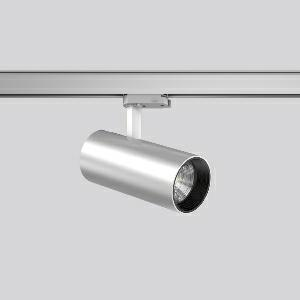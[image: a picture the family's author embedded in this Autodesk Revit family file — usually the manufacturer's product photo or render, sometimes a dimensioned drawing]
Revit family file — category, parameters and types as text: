
# Revit family: deecos_s_mini_742199_004_1_76_ead4
name_source: partatom
category: Lighting Fixtures
units: mm (PartAtom-declared; Revit-internal decimal feet)

## family parameters
Cut with Voids When Loaded = No
Host = Face
Light Source = No
Part Type = Normal
Room Calculation Point = No
Round Connector Dimension = Use Diameter
Shared = No

## types (1)
- DEECOS S mini (1 x LED Modul 940, 2250 lm, 4000)
    Apparent Load = 20 VA
    Approval mark = CE
    CIE Flux Codes = 96 100 100 100 100
    Color Rendering = 92
    Color Temperature = 4000
    Default Elevation = 1800 mm
    Description = Series: DEECOS S mini
LED surface-mounted projector in modern design with no visible cooling ribs. Housing: die-cast aluminium, powder-coated. Rotation range: 356°. Swivel range: 90°. Black plastic ring and recessed LED to prevent glare from the side. Optical assembly with lens made of plastic (polycarbonate) for the best homogeneous light distribution - can be changed without tools. Best colour rendering index Ra>90. With adapter for RZB 3-circuit DALI tracks. Suitable for Track on ceiling, Wall track. High quality converter without flickering and stroboscopic effect. The following accessories can be mounted without use of tools: interchangeable lenses, decorative glasses, honeycomb louvre, clear and frosted diffusers, white interchangeable plastic ring. 
Colour: silver
Diameter: 87 mm
Height: 214 mm
Lamp: LED
Socket: without socket
Colour temperature: 4000K
Colour rendering index (CRI): 92
System power: 20 W
Rated luminous flux: 2250 lm
Luminous efficiency: 113 lm/W
Control gear: Converter, dimmable, DALI
Protection class: I
Type of protection: IP 20
    Height = 214 mm
    Lamp = 1 x LED Modul 940
    Lamp Light Flux = 2250 lm
    Lamp count = 1
    Length = 87 mm
    Lifetime = 50000 h
    Luminous efficacy = 113 lm/W
    Manufacturer = RZB
    ModVariant = No
    Model = 742199.004.1.76
    Mounting Place = Ceiling
    Mounting Type = Rail mounted
    Number of Poles = 1
    OnlyDefault = Yes
    Power Factor = 1
    Product Name = DEECOS S mini
    Product group = Track mounted projectors
    ProductGroupID = 301
    Protection Class = Protection class I
    Protection Degree = IP 20
    RLX_Detail_Level = 1
    RLX_Emergency_Light_Flux = 0 lm
    RLX_Emergency_Type = 0
    RLX_Emergency_Type_DB = No
    RlxData = <blob elided: 37613 chars, md5=c1aae286>
    Socket = socket
    Standby Power = 0 W
    System Light Flux = 2250 lm
    System Power = 20 W
    Type Comments = Product without accessories
    Type Image = 741930.004.jpg
    URL = http://relux.com
    VarID = ---
    Voltage = 230 V
    Voltage Range = 220-240 V
    Weight = 0.00 kg
    Width = 0 mm  [stored 0 ft]

note: [stored X ft] marks values corroborated as IEEE doubles in the binary element streams (Revit-internal decimal feet)

## geometry (parser evidence)
native form markers: Blend x4, Sweep x14
no freeform markers — native parametric forms only
